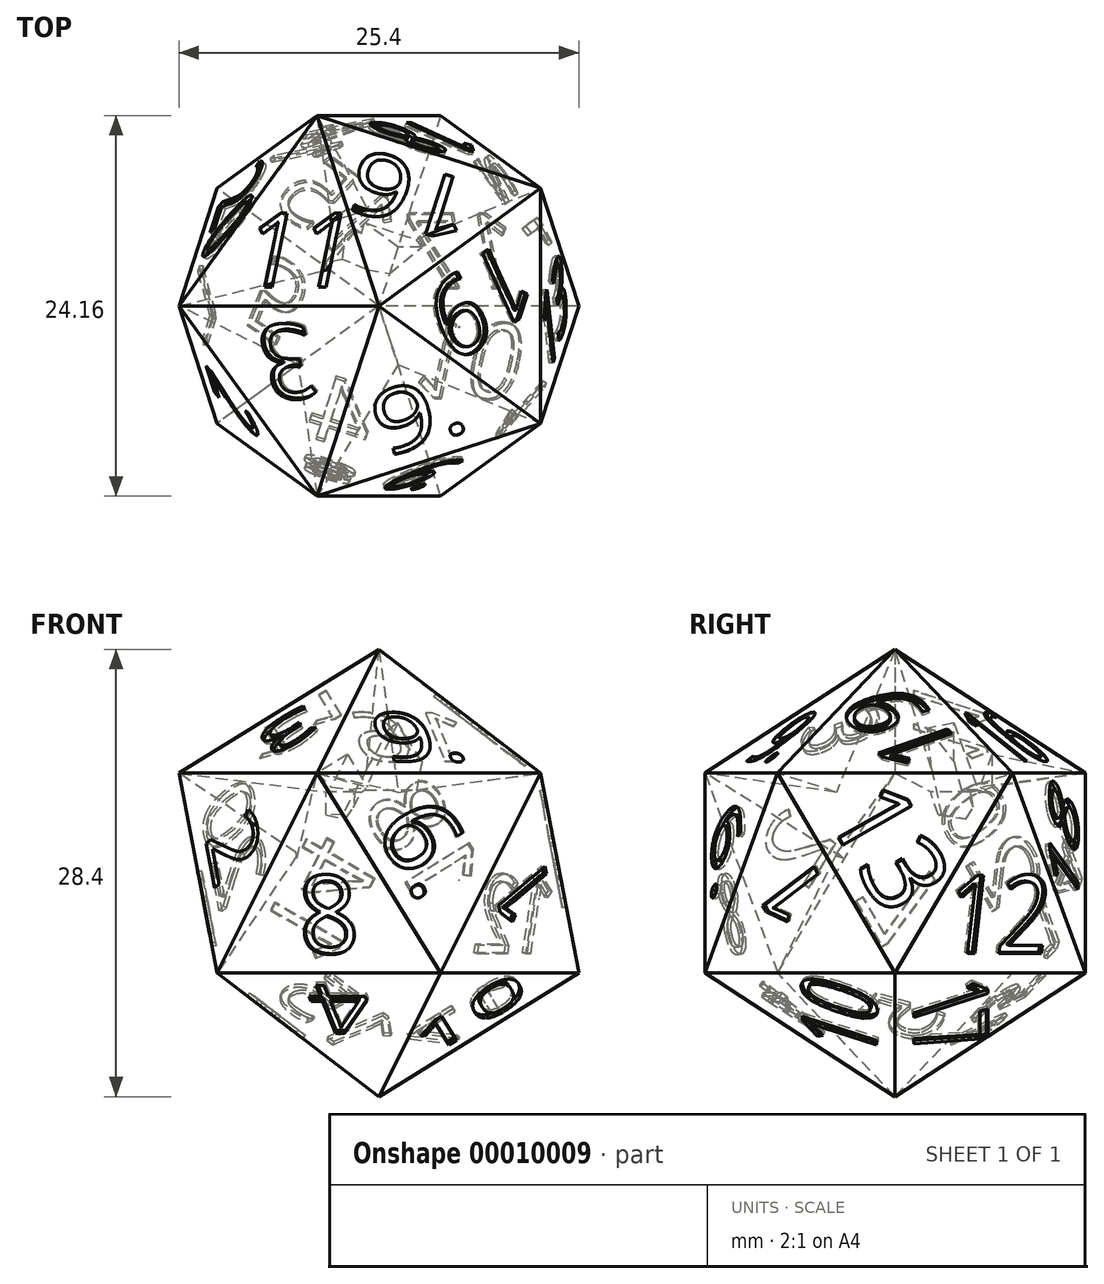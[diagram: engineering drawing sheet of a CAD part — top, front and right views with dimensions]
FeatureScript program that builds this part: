
annotation { "Feature Type Name" : "Feature", "Feature Type Description" : "" }
export const myFeature = defineFeature(function(context is Context, id is Id, definition is map)
    precondition{}
    {
        {
            var Q0;
            Q0=qCreatedBy(makeId("Top.planeOp"),FACE);
            var sketch = newSketch(context, id + "F0", { "sketchPlane" : qUnion([Q0])});
            skCircle(sketch, "E0.cCircle", {"center": v(0, 0) * mm, "radius": 12.7 * mm, "construction": true});
            skLineSegment(sketch, "E0.0", {"start": v(10.27, 7.46) * mm, "end": v(10.27, -7.46) * mm});
            skLineSegment(sketch, "E0.1", {"start": v(10.27, -7.46) * mm, "end": v(-3.92, -12.08) * mm});
            skLineSegment(sketch, "E0.2", {"start": v(-3.92, -12.08) * mm, "end": v(-12.7, 0) * mm});
            skLineSegment(sketch, "E0.3", {"start": v(-12.7, 0) * mm, "end": v(-3.92, 12.08) * mm});
            skLineSegment(sketch, "E0.4", {"start": v(-3.92, 12.08) * mm, "end": v(10.27, 7.46) * mm});
            skLineSegment(sketch, "E1", {"start": v(0, 0) * mm, "end": v(-3.92, -12.08) * mm, "construction": true});
            skSolve(sketch);
        }
        {
            var Q0;
            Q0=qCreatedBy(makeId("Right.planeOp"),FACE);
            var sketch = newSketch(context, id + "F1", { "sketchPlane" : qUnion([Q0])});
            skLineSegment(sketch, "E2", {"start": v(0, 0) * mm, "end": v(0, 7.85) * mm, "construction": true});
            skSolve(sketch);
        }
        {
            var Q0;
            Q0=sQuery(id+"F0.wireOp",VERTEX,"E0.1.start");
            var Q1;
            Q1=sQuery(id+"F0.wireOp",VERTEX,"E0.2.start");
            var Q2;
            Q2=sQuery(id+"F1.wireOp",VERTEX,"E2.end");
            cPlane(context, id + "F2", {"entities" : qUnion([Q0, Q1, Q2]), "cplaneType" : CPlaneType.THREE_POINT, "offset" : 152.4 * mm, "width" : 152.4 * mm, "height" : 152.4 * mm});
        }
        {
            var Q0;
            Q0=qCreatedBy(id+"F2.planeOp",FACE);
            var sketch = newSketch(context, id + "F3", { "sketchPlane" : qUnion([Q0])});
            skPoint(sketch, "E3.0", {"position": v(-5.19, -9.77) * mm});
            skPoint(sketch, "E4.0", {"position": v(9.27, -6.04) * mm});
            skPoint(sketch, "E5.0", {"position": v(-1.2, 4.61) * mm});
            skLineSegment(sketch, "E6", {"start": v(-5.19, -9.77) * mm, "end": v(-1.2, 4.61) * mm});
            skLineSegment(sketch, "E7", {"start": v(9.27, -6.04) * mm, "end": v(-1.2, 4.61) * mm});
            skLineSegment(sketch, "E8", {"start": v(9.27, -6.04) * mm, "end": v(-5.19, -9.77) * mm});
            skLineSegment(sketch, "E9", {"start": v(-3.19, -2.58) * mm, "end": v(9.27, -6.04) * mm, "construction": true});
            skSolve(sketch);
        }
        {
            var Q0;
            Q0=sQuery(id+"F3.wireOp",VERTEX,"E3.0");
            var Q1;
            Q1=sQuery(id+"F0.wireOp",VERTEX,"E0.2.end");
            var Q2;
            Q2=sQuery(id+"F1.wireOp",VERTEX,"E2.end");
            cPlane(context, id + "F4", {"entities" : qUnion([Q0, Q1, Q2]), "cplaneType" : CPlaneType.THREE_POINT, "offset" : 152.4 * mm, "width" : 152.4 * mm, "height" : 152.4 * mm});
        }
        {
            var Q0;
            Q0=qCreatedBy(id+"F4.planeOp",FACE);
            var sketch = newSketch(context, id + "F5", { "sketchPlane" : qUnion([Q0])});
            skPoint(sketch, "E10.0", {"position": v(-11.06, 0) * mm});
            skPoint(sketch, "E11.0", {"position": v(-0.99, -11.02) * mm});
            skPoint(sketch, "E12.0", {"position": v(3.52, 3.21) * mm});
            skLineSegment(sketch, "E13", {"start": v(-11.06, 0) * mm, "end": v(3.52, 3.21) * mm});
            skLineSegment(sketch, "E14", {"start": v(-0.99, -11.02) * mm, "end": v(-11.06, 0) * mm});
            skLineSegment(sketch, "E15", {"start": v(-0.99, -11.02) * mm, "end": v(3.52, 3.21) * mm});
            skLineSegment(sketch, "E16", {"start": v(-11.06, 0) * mm, "end": v(1.26, -3.9) * mm, "construction": true});
            skLineSegment(sketch, "E17", {"start": v(3.52, 3.21) * mm, "end": v(-6.03, -5.5) * mm, "construction": true});
            skSolve(sketch);
        }
        {
            var Q0;
            Q0=sQuery(id+"F5.wireOp",VERTEX,"E10.0");
            var Q1;
            Q1=sQuery(id+"F0.wireOp",VERTEX,"E0.3.end");
            var Q2;
            Q2=sQuery(id+"F3.wireOp",VERTEX,"E5.0");
            cPlane(context, id + "F6", {"entities" : qUnion([Q0, Q1, Q2]), "cplaneType" : CPlaneType.THREE_POINT, "offset" : 152.4 * mm, "width" : 152.4 * mm, "height" : 152.4 * mm});
        }
        {
            var Q0;
            Q0=qCreatedBy(id+"F6.planeOp",FACE);
            var sketch = newSketch(context, id + "F7", { "sketchPlane" : qUnion([Q0])});
            skPoint(sketch, "E18.0", {"position": v(-0.99, 11.02) * mm});
            skPoint(sketch, "E19.0", {"position": v(-11.06, 0) * mm});
            skPoint(sketch, "E20.0", {"position": v(3.52, -3.21) * mm});
            skLineSegment(sketch, "E21", {"start": v(-0.99, 11.02) * mm, "end": v(3.52, -3.21) * mm});
            skLineSegment(sketch, "E22", {"start": v(3.52, -3.21) * mm, "end": v(-11.06, 0) * mm});
            skLineSegment(sketch, "E23", {"start": v(-0.99, 11.02) * mm, "end": v(-11.06, 0) * mm});
            skLineSegment(sketch, "E24", {"start": v(-6.03, 5.5) * mm, "end": v(3.52, -3.21) * mm, "construction": true});
            skSolve(sketch);
        }
        {
            var Q0;
            Q0=sQuery(id+"F0.wireOp",VERTEX,"E0.4.end");
            var Q1;
            Q1=sQuery(id+"F3.wireOp",VERTEX,"E5.0");
            var Q2;
            Q2=sQuery(id+"F0.wireOp",VERTEX,"E0.3.end");
            cPlane(context, id + "F8", {"entities" : qUnion([Q0, Q1, Q2]), "cplaneType" : CPlaneType.THREE_POINT, "offset" : 152.4 * mm, "width" : 152.4 * mm, "height" : 152.4 * mm});
        }
        {
            var Q0;
            Q0=qCreatedBy(id+"F8.planeOp",FACE);
            var sketch = newSketch(context, id + "F9", { "sketchPlane" : qUnion([Q0])});
            skPoint(sketch, "E25.0", {"position": v(-5.19, 9.77) * mm});
            skPoint(sketch, "E26.0", {"position": v(9.27, 6.04) * mm});
            skPoint(sketch, "E27.0", {"position": v(-1.2, -4.61) * mm});
            skLineSegment(sketch, "E28", {"start": v(9.27, 6.04) * mm, "end": v(-1.2, -4.61) * mm});
            skLineSegment(sketch, "E29", {"start": v(-1.2, -4.61) * mm, "end": v(-5.19, 9.77) * mm});
            skLineSegment(sketch, "E30", {"start": v(-5.19, 9.77) * mm, "end": v(9.27, 6.04) * mm});
            skSolve(sketch);
        }
        {
            var Q0;
            Q0=sQuery(id+"F0.wireOp",VERTEX,"E0.4.end");
            var Q1;
            Q1=sQuery(id+"F3.wireOp",VERTEX,"E5.0");
            var Q2;
            Q2=sQuery(id+"F3.wireOp",VERTEX,"E4.0");
            cPlane(context, id + "F10", {"entities" : qUnion([Q0, Q1, Q2]), "cplaneType" : CPlaneType.THREE_POINT, "offset" : 152.4 * mm, "width" : 152.4 * mm, "height" : 152.4 * mm});
        }
        {
            var Q0;
            Q0=qCreatedBy(id+"F10.planeOp",FACE);
            var sketch = newSketch(context, id + "F11", { "sketchPlane" : qUnion([Q0])});
            skPoint(sketch, "E31.0", {"position": v(8.16, 7.46) * mm});
            skPoint(sketch, "E32.0", {"position": v(-4.76, 0) * mm});
            skPoint(sketch, "E33.0", {"position": v(8.16, -7.46) * mm});
            skLineSegment(sketch, "E34", {"start": v(8.16, 7.46) * mm, "end": v(8.16, -7.46) * mm});
            skLineSegment(sketch, "E35", {"start": v(8.16, -7.46) * mm, "end": v(-4.76, 0) * mm});
            skLineSegment(sketch, "E36", {"start": v(8.16, 7.46) * mm, "end": v(-4.76, 0) * mm});
            skSolve(sketch);
        }
        {
            var Q0;
            Q0=sQuery(id+"F5.wireOp",EDGE,"E14");
            cPlane(context, id + "F12", {"entities" : qUnion([Q0]), "cplaneType" : CPlaneType.LINE_ANGLE, "offset" : 152.4 * mm, "angle" : 100.81 * degree, "width" : 152.4 * mm, "height" : 152.4 * mm});
        }
        {
            var Q0;
            Q0=qCreatedBy(id+"F12.planeOp",FACE);
            var sketch = newSketch(context, id + "F13", { "sketchPlane" : qUnion([Q0])});
            skLineSegment(sketch, "E37", {"start": v(7.14, -2.92) * mm, "end": v(-7.66, -0.9) * mm});
            skPoint(sketch, "E38.orphan", {"position": v(-2, -14.73) * mm});
            skPoint(sketch, "E39.start.orphan", {"position": v(-0.26, -1.91) * mm});
            skPoint(sketch, "E40.start.orphan", {"position": v(2.56, -8.82) * mm});
            skLineSegment(sketch, "E41", {"start": v(7.14, -2.92) * mm, "end": v(-2, -14.72) * mm});
            skLineSegment(sketch, "E42", {"start": v(-7.66, -0.9) * mm, "end": v(-2, -14.72) * mm});
            skLineSegment(sketch, "E43", {"start": v(-0.26, -1.91) * mm, "end": v(-2, -14.72) * mm, "construction": true});
            skLineSegment(sketch, "E44", {"start": v(-4.83, -7.81) * mm, "end": v(7.14, -2.92) * mm, "construction": true});
            skSolve(sketch);
        }
        {
            var Q0;
            Q0=makeQuery(id+"F7.imprint","IMPRINT",FACE,{"disambiguationData":[TD([[makeQuery(id+"F7.imprint","IMPRINT",EDGE,{"derivedFrom":sQuery(id+"F7.wireOp",EDGE,"E21")}),-1.0]])]});
            extrude(context, id + "F14", {"entities" : qUnion([Q0]), "oppositeDirection" : true, "depth" : 2 / 76.2 * mm});
        }
        {
            var Q0;
            Q0=makeQuery(id+"F9.imprint","IMPRINT",FACE,{"disambiguationData":[TD([[makeQuery(id+"F9.imprint","IMPRINT",EDGE,{"derivedFrom":sQuery(id+"F9.wireOp",EDGE,"E28")}),-1.0]])]});
            extrude(context, id + "F15", {"entities" : qUnion([Q0]), "operationType" : NewBodyOperationType.ADD, "oppositeDirection" : true, "depth" : 2 / 76.2 * mm});
        }
        {
            var Q0;
            Q0=makeQuery(id+"F11.imprint","IMPRINT",FACE,{"disambiguationData":[TD([[makeQuery(id+"F11.imprint","IMPRINT",EDGE,{"derivedFrom":sQuery(id+"F11.wireOp",EDGE,"E34")}),-1.0]])]});
            extrude(context, id + "F16", {"entities" : qUnion([Q0]), "operationType" : NewBodyOperationType.ADD, "depth" : 16.93 * mm});
        }
        {
            var Q0;
            Q0=makeQuery(id+"F3.imprint","IMPRINT",FACE,{"disambiguationData":[TD([[makeQuery(id+"F3.imprint","IMPRINT",EDGE,{"derivedFrom":sQuery(id+"F3.wireOp",EDGE,"E6")}),-1.0]])]});
            extrude(context, id + "F17", {"entities" : qUnion([Q0]), "operationType" : NewBodyOperationType.ADD, "oppositeDirection" : true, "depth" : 2 / 76.2 * mm});
        }
        {
            var Q0;
            Q0=makeQuery(id+"F5.imprint","IMPRINT",FACE,{"disambiguationData":[TD([[makeQuery(id+"F5.imprint","IMPRINT",EDGE,{"derivedFrom":sQuery(id+"F5.wireOp",EDGE,"E13")}),-1.0]])]});
            extrude(context, id + "F18", {"entities" : qUnion([Q0]), "operationType" : NewBodyOperationType.ADD, "oppositeDirection" : true, "depth" : 18.55 * mm});
        }
        {
            var Q0;
            Q0 = qSketchRegion(id + "F13", true);
            extrude(context, id + "F19", {"entities" : qUnion([Q0]), "operationType" : NewBodyOperationType.ADD, "depth" : 2 / 76.2 * mm});
        }
        {
            var Q0;
            Q0=makeQuery(id+"F19.opExtrude","CAP_EDGE",EDGE,{"disambiguationData":[OSD([sQuery(id+"F13.wireOp",EDGE,"E42")])],"isStart":true});
            cPlane(context, id + "F20", {"entities" : qUnion([Q0]), "cplaneType" : CPlaneType.LINE_ANGLE, "offset" : 152.4 * mm, "angle" : 100.81 * degree, "width" : 152.4 * mm, "height" : 152.4 * mm});
        }
        {
            var Q0;
            Q0=qCreatedBy(id+"F20.planeOp",FACE);
            var sketch = newSketch(context, id + "F21", { "sketchPlane" : qUnion([Q0])});
            skLineSegment(sketch, "E45.0", {"start": v(0.15, 2.38) * mm, "end": v(6.81, -10.98) * mm});
            skLineSegment(sketch, "E46", {"start": v(6.81, -10.98) * mm, "end": v(-8.1, -10.07) * mm});
            skLineSegment(sketch, "E47", {"start": v(-8.1, -10.07) * mm, "end": v(0.15, 2.38) * mm});
            skLineSegment(sketch, "E48", {"start": v(-8.1, -10.07) * mm, "end": v(3.48, -4.3) * mm, "construction": true});
            skSolve(sketch);
        }
        {
            var Q0;
            Q0 = qSketchRegion(id + "F21", true);
            extrude(context, id + "F22", {"entities" : qUnion([Q0]), "operationType" : NewBodyOperationType.ADD, "depth" : 16.93 * mm});
        }
        {
            var Q0;
            Q0=sQuery(id+"F5.wireOp",VERTEX,"E11.0");
            var Q1;
            Q1=sQuery(id+"F3.wireOp",VERTEX,"E4.0");
            var Q2;
            Q2=makeQuery(id+"F22.opExtrude","CAP_VERTEX",VERTEX,{"disambiguationData":[OSD([sQuery(id+"F21.wireOp",EDGE,"E46"),sQuery(id+"F21.wireOp",EDGE,"E47")])],"isStart":true});
            cPlane(context, id + "F23", {"entities" : qUnion([Q0, Q1, Q2]), "cplaneType" : CPlaneType.THREE_POINT, "offset" : 152.4 * mm, "width" : 152.4 * mm, "height" : 152.4 * mm});
        }
        {
            var Q0;
            Q0=qCreatedBy(id+"F23.planeOp",FACE);
            var sketch = newSketch(context, id + "F24", { "sketchPlane" : qUnion([Q0])});
            skLineSegment(sketch, "E49.0", {"start": v(0.9, -14.83) * mm, "end": v(-7.33, -2.38) * mm});
            skLineSegment(sketch, "E50.0", {"start": v(7.57, -1.47) * mm, "end": v(-7.33, -2.38) * mm});
            skLineSegment(sketch, "E51", {"start": v(0.9, -14.83) * mm, "end": v(7.57, -1.47) * mm});
            skLineSegment(sketch, "E52", {"start": v(4.24, -8.15) * mm, "end": v(-7.33, -2.38) * mm, "construction": true});
            skSolve(sketch);
        }
        {
            var Q0;
            Q0=makeQuery(id+"F24.imprint","IMPRINT",FACE,{"disambiguationData":[TD([[makeQuery(id+"F24.imprint","IMPRINT",EDGE,{"derivedFrom":sQuery(id+"F24.wireOp",EDGE,"E49.0")}),-1.0]])]});
            extrude(context, id + "F25", {"entities" : qUnion([Q0]), "operationType" : NewBodyOperationType.ADD, "oppositeDirection" : true, "depth" : 16.93 * mm});
        }
        {
            var Q0;
            Q0=makeQuery(id+"F14.opExtrude","CAP_EDGE",EDGE,{"disambiguationData":[OSD([sQuery(id+"F7.wireOp",EDGE,"E23")])],"isStart":true});
            cPlane(context, id + "F26", {"entities" : qUnion([Q0]), "cplaneType" : CPlaneType.LINE_ANGLE, "offset" : 152.4 * mm, "angle" : 79.18 * degree, "width" : 152.4 * mm, "height" : 152.4 * mm});
        }
        {
            var Q0;
            Q0=qCreatedBy(id+"F26.planeOp",FACE);
            var sketch = newSketch(context, id + "F27", { "sketchPlane" : qUnion([Q0])});
            skLineSegment(sketch, "E53.0", {"start": v(7.66, -0.9) * mm, "end": v(-7.14, -2.92) * mm});
            skLineSegment(sketch, "E54", {"start": v(7.66, -0.9) * mm, "end": v(2, -14.72) * mm});
            skLineSegment(sketch, "E55", {"start": v(2, -14.72) * mm, "end": v(-7.14, -2.92) * mm});
            skLineSegment(sketch, "E56", {"start": v(2, -14.72) * mm, "end": v(0.26, -1.91) * mm, "construction": true});
            skLineSegment(sketch, "E57", {"start": v(4.83, -7.81) * mm, "end": v(-7.14, -2.92) * mm, "construction": true});
            skSolve(sketch);
        }
        {
            var Q0;
            Q0 = qSketchRegion(id + "F27", true);
            extrude(context, id + "F28", {"entities" : qUnion([Q0]), "operationType" : NewBodyOperationType.ADD, "depth" : 6.35 * mm});
        }
        {
            var Q0;
            Q0=sQuery(id+"F7.wireOp",VERTEX,"E19.0");
            var Q1;
            Q1=makeQuery(id+"F22.boolean.opBoolean","MERGE",VERTEX,{"derivedFrom":[makeQuery(id+"F19.opExtrude","CAP_VERTEX",VERTEX,{"disambiguationData":[OSD([sQuery(id+"F13.wireOp",EDGE,"E41"),sQuery(id+"F13.wireOp",EDGE,"E42")])],"isStart":true}),makeQuery(id+"F22.opExtrude","CAP_VERTEX",VERTEX,{"disambiguationData":[OSD([sQuery(id+"F21.wireOp",EDGE,"E45.0"),sQuery(id+"F21.wireOp",EDGE,"E46")])],"isStart":true})]});
            var Q2;
            Q2=sQuery(id+"F27.wireOp",VERTEX,"E54.end");
            cPlane(context, id + "F29", {"entities" : qUnion([Q0, Q1, Q2]), "cplaneType" : CPlaneType.THREE_POINT, "offset" : 152.4 * mm, "width" : 152.4 * mm, "height" : 152.4 * mm});
        }
        {
            var Q0;
            Q0=qCreatedBy(id+"F29.planeOp",FACE);
            var sketch = newSketch(context, id + "F30", { "sketchPlane" : qUnion([Q0])});
            skLineSegment(sketch, "E58.0", {"start": v(0, 2.38) * mm, "end": v(7.46, -10.55) * mm});
            skLineSegment(sketch, "E59.0", {"start": v(-7.47, -10.55) * mm, "end": v(0, 2.38) * mm});
            skLineSegment(sketch, "E60", {"start": v(-7.47, -10.55) * mm, "end": v(7.46, -10.55) * mm});
            skSolve(sketch);
        }
        {
            var Q0;
            Q0=makeQuery(id+"F30.imprint","IMPRINT",FACE,{"disambiguationData":[TD([[makeQuery(id+"F30.imprint","IMPRINT",EDGE,{"derivedFrom":sQuery(id+"F30.wireOp",EDGE,"E58.0")}),-1.0]])]});
            extrude(context, id + "F31", {"entities" : qUnion([Q0]), "operationType" : NewBodyOperationType.ADD, "oppositeDirection" : true, "depth" : 6.35 * mm});
        }
        {
            var Q0;
            Q0=sQuery(id+"F27.wireOp",EDGE,"E54");
            cPlane(context, id + "F32", {"entities" : qUnion([Q0]), "cplaneType" : CPlaneType.LINE_ANGLE, "offset" : 152.4 * mm, "angle" : 79.19 * degree, "width" : 152.4 * mm, "height" : 152.4 * mm});
        }
        {
            var Q0;
            Q0=qCreatedBy(id+"F32.planeOp",FACE);
            var sketch = newSketch(context, id + "F33", { "sketchPlane" : qUnion([Q0])});
            skLineSegment(sketch, "E61.0", {"start": v(0.15, 2.38) * mm, "end": v(6.81, -10.98) * mm});
            skLineSegment(sketch, "E62", {"start": v(0.15, 2.38) * mm, "end": v(-8.1, -10.08) * mm});
            skLineSegment(sketch, "E63", {"start": v(-8.1, -10.08) * mm, "end": v(6.81, -10.98) * mm});
            skLineSegment(sketch, "E64", {"start": v(-8.1, -10.08) * mm, "end": v(3.48, -4.3) * mm, "construction": true});
            skLineSegment(sketch, "E65", {"start": v(0.15, 2.38) * mm, "end": v(-0.64, -10.53) * mm, "construction": true});
            skSolve(sketch);
        }
        {
            var Q0;
            Q0 = qSketchRegion(id + "F33", true);
            extrude(context, id + "F34", {"entities" : qUnion([Q0]), "operationType" : NewBodyOperationType.ADD, "oppositeDirection" : true, "depth" : 6.35 * mm});
        }
        {
            var Q0;
            Q0=sQuery(id+"F33.wireOp",EDGE,"E63");
            cPlane(context, id + "F35", {"entities" : qUnion([Q0]), "cplaneType" : CPlaneType.LINE_ANGLE, "offset" : 152.4 * mm, "angle" : 52.62 * degree, "width" : 152.4 * mm, "height" : 152.4 * mm});
        }
        {
            var Q0;
            Q0=qCreatedBy(id+"F35.planeOp",FACE);
            var sketch = newSketch(context, id + "F36", { "sketchPlane" : qUnion([Q0])});
            skLineSegment(sketch, "E66.0", {"start": v(7.11, 2.3) * mm, "end": v(-7.34, -1.43) * mm});
            skLineSegment(sketch, "E67", {"start": v(7.11, 2.3) * mm, "end": v(3.12, -12.08) * mm});
            skLineSegment(sketch, "E68", {"start": v(3.12, -12.08) * mm, "end": v(-7.34, -1.43) * mm});
            skLineSegment(sketch, "E69", {"start": v(-0.11, 0.44) * mm, "end": v(3.12, -12.08) * mm, "construction": true});
            skLineSegment(sketch, "E70", {"start": v(-7.34, -1.43) * mm, "end": v(5.12, -4.89) * mm, "construction": true});
            skSolve(sketch);
        }
        {
            var Q0;
            Q0 = qSketchRegion(id + "F36", true);
            extrude(context, id + "F37", {"entities" : qUnion([Q0]), "operationType" : NewBodyOperationType.ADD, "depth" : 6.35 * mm});
        }
        {
            var Q0;
            Q0=sQuery(id+"F36.wireOp",EDGE,"E67");
            cPlane(context, id + "F38", {"entities" : qUnion([Q0]), "cplaneType" : CPlaneType.LINE_ANGLE, "offset" : 152.4 * mm, "angle" : 30.6 * degree, "width" : 152.4 * mm, "height" : 152.4 * mm});
        }
        {
            var Q0;
            Q0=qCreatedBy(id+"F38.planeOp",FACE);
            var sketch = newSketch(context, id + "F39", { "sketchPlane" : qUnion([Q0])});
            skLineSegment(sketch, "E71.0", {"start": v(-4.7, -5.82) * mm, "end": v(-9.2, 8.42) * mm});
            skLineSegment(sketch, "E72", {"start": v(-4.7, -5.82) * mm, "end": v(5.37, 5.2) * mm});
            skLineSegment(sketch, "E73", {"start": v(5.37, 5.2) * mm, "end": v(-9.2, 8.42) * mm});
            skLineSegment(sketch, "E74", {"start": v(-6.96, 1.3) * mm, "end": v(5.37, 5.2) * mm, "construction": true});
            skSolve(sketch);
        }
        {
            var Q0;
            Q0 = qSketchRegion(id + "F39", true);
            extrude(context, id + "F40", {"entities" : qUnion([Q0]), "operationType" : NewBodyOperationType.ADD, "oppositeDirection" : true, "depth" : 6.35 * mm});
        }
        {
            var Q0;
            Q0=sQuery(id+"F36.wireOp",VERTEX,"E66.0.start");
            var Q1;
            Q1=makeQuery(id+"F34.boolean.opBoolean","MERGE",VERTEX,{"derivedFrom":[makeQuery(id+"F28.boolean.opBoolean","MERGE",VERTEX,{"derivedFrom":[makeQuery(id+"F15.boolean.opBoolean","MERGE",VERTEX,{"derivedFrom":[makeQuery(id+"F14.opExtrude","CAP_VERTEX",VERTEX,{"disambiguationData":[OSD([sQuery(id+"F7.wireOp",EDGE,"E21"),sQuery(id+"F7.wireOp",EDGE,"E23")])],"isStart":true}),makeQuery(id+"F15.opExtrude","CAP_VERTEX",VERTEX,{"disambiguationData":[OSD([sQuery(id+"F9.wireOp",EDGE,"E29"),sQuery(id+"F9.wireOp",EDGE,"E30")])],"isStart":true})]}),makeQuery(id+"F28.opExtrude","CAP_VERTEX",VERTEX,{"disambiguationData":[OSD([sQuery(id+"F27.wireOp",EDGE,"E53.0"),sQuery(id+"F27.wireOp",EDGE,"E54")])],"isStart":true})]}),makeQuery(id+"F34.opExtrude","CAP_VERTEX",VERTEX,{"disambiguationData":[OSD([sQuery(id+"F33.wireOp",EDGE,"E61.0"),sQuery(id+"F33.wireOp",EDGE,"E62")])],"isStart":true})]});
            var Q2;
            Q2=makeQuery(id+"F16.boolean.opBoolean","MERGE",VERTEX,{"derivedFrom":[makeQuery(id+"F15.opExtrude","CAP_VERTEX",VERTEX,{"disambiguationData":[OSD([sQuery(id+"F9.wireOp",EDGE,"E28"),sQuery(id+"F9.wireOp",EDGE,"E30")])],"isStart":true}),makeQuery(id+"F16.opExtrude","CAP_VERTEX",VERTEX,{"disambiguationData":[OSD([sQuery(id+"F11.wireOp",EDGE,"E34"),sQuery(id+"F11.wireOp",EDGE,"E35")])],"isStart":true})]});
            cPlane(context, id + "F41", {"entities" : qUnion([Q0, Q1, Q2]), "cplaneType" : CPlaneType.THREE_POINT, "offset" : 152.4 * mm, "width" : 152.4 * mm, "height" : 152.4 * mm});
        }
        {
            var Q0;
            Q0=qCreatedBy(id+"F41.planeOp",FACE);
            var sketch = newSketch(context, id + "F42", { "sketchPlane" : qUnion([Q0])});
            skLineSegment(sketch, "E75.0", {"start": v(-7.33, -2.38) * mm, "end": v(7.57, -1.47) * mm});
            skLineSegment(sketch, "E76.0", {"start": v(-7.33, -2.38) * mm, "end": v(0.9, -14.83) * mm});
            skLineSegment(sketch, "E77", {"start": v(0.9, -14.83) * mm, "end": v(7.57, -1.47) * mm});
            skSolve(sketch);
        }
        {
            var Q0;
            Q0 = qSketchRegion(id + "F42", true);
            extrude(context, id + "F43", {"entities" : qUnion([Q0]), "operationType" : NewBodyOperationType.ADD, "depth" : 6.35 * mm});
        }
        {
            var Q0;
            Q0=sQuery(id+"F36.wireOp",VERTEX,"E66.0.start");
            var Q1;
            Q1=makeQuery(id+"F40.opExtrude","CAP_VERTEX",VERTEX,{"disambiguationData":[OSD([sQuery(id+"F39.wireOp",EDGE,"E72"),sQuery(id+"F39.wireOp",EDGE,"E73")])],"isStart":true});
            var Q2;
            Q2=makeQuery(id+"F43.boolean.opBoolean","MERGE",VERTEX,{"derivedFrom":[makeQuery(id+"F16.boolean.opBoolean","MERGE",VERTEX,{"derivedFrom":[makeQuery(id+"F15.opExtrude","CAP_VERTEX",VERTEX,{"disambiguationData":[OSD([sQuery(id+"F9.wireOp",EDGE,"E28"),sQuery(id+"F9.wireOp",EDGE,"E30")])],"isStart":true}),makeQuery(id+"F16.opExtrude","CAP_VERTEX",VERTEX,{"disambiguationData":[OSD([sQuery(id+"F11.wireOp",EDGE,"E34"),sQuery(id+"F11.wireOp",EDGE,"E35")])],"isStart":true})]}),makeQuery(id+"F43.opExtrude","CAP_VERTEX",VERTEX,{"disambiguationData":[OSD([sQuery(id+"F42.wireOp",EDGE,"E75.0"),sQuery(id+"F42.wireOp",EDGE,"E77")])],"isStart":true})]});
            cPlane(context, id + "F44", {"entities" : qUnion([Q0, Q1, Q2]), "cplaneType" : CPlaneType.THREE_POINT, "offset" : 152.4 * mm, "width" : 152.4 * mm, "height" : 152.4 * mm});
        }
        {
            var Q0;
            Q0=qCreatedBy(id+"F44.planeOp",FACE);
            var sketch = newSketch(context, id + "F45", { "sketchPlane" : qUnion([Q0])});
            skLineSegment(sketch, "E78.0", {"start": v(5.97, -11.46) * mm, "end": v(0.32, 2.36) * mm});
            skLineSegment(sketch, "E79.0", {"start": v(5.97, -11.46) * mm, "end": v(-8.82, -9.44) * mm});
            skLineSegment(sketch, "E80", {"start": v(0.32, 2.36) * mm, "end": v(-8.82, -9.44) * mm});
            skSolve(sketch);
        }
        {
            var Q0;
            Q0 = qSketchRegion(id + "F45", true);
            extrude(context, id + "F46", {"entities" : qUnion([Q0]), "operationType" : NewBodyOperationType.ADD, "oppositeDirection" : true, "depth" : 6.35 * mm});
        }
        {
            var Q0;
            Q0=makeQuery(id+"F46.boolean.opBoolean","MERGE",VERTEX,{"derivedFrom":[makeQuery(id+"F40.opExtrude","CAP_VERTEX",VERTEX,{"disambiguationData":[OSD([sQuery(id+"F39.wireOp",EDGE,"E72"),sQuery(id+"F39.wireOp",EDGE,"E73")])],"isStart":true}),makeQuery(id+"F46.opExtrude","CAP_VERTEX",VERTEX,{"disambiguationData":[OSD([sQuery(id+"F45.wireOp",EDGE,"E79.0"),sQuery(id+"F45.wireOp",EDGE,"E80")])],"isStart":true})]});
            var Q1;
            Q1=makeQuery(id+"F46.boolean.opBoolean","MERGE",VERTEX,{"derivedFrom":[makeQuery(id+"F43.boolean.opBoolean","MERGE",VERTEX,{"derivedFrom":[makeQuery(id+"F16.boolean.opBoolean","MERGE",VERTEX,{"derivedFrom":[makeQuery(id+"F15.opExtrude","CAP_VERTEX",VERTEX,{"disambiguationData":[OSD([sQuery(id+"F9.wireOp",EDGE,"E28"),sQuery(id+"F9.wireOp",EDGE,"E30")])],"isStart":true}),makeQuery(id+"F16.opExtrude","CAP_VERTEX",VERTEX,{"disambiguationData":[OSD([sQuery(id+"F11.wireOp",EDGE,"E34"),sQuery(id+"F11.wireOp",EDGE,"E35")])],"isStart":true})]}),makeQuery(id+"F43.opExtrude","CAP_VERTEX",VERTEX,{"disambiguationData":[OSD([sQuery(id+"F42.wireOp",EDGE,"E75.0"),sQuery(id+"F42.wireOp",EDGE,"E77")])],"isStart":true})]}),makeQuery(id+"F46.opExtrude","CAP_VERTEX",VERTEX,{"disambiguationData":[OSD([sQuery(id+"F45.wireOp",EDGE,"E78.0"),sQuery(id+"F45.wireOp",EDGE,"E80")])],"isStart":true})]});
            var Q2;
            Q2=makeQuery(id+"F25.boolean.opBoolean","MERGE",VERTEX,{"derivedFrom":[makeQuery(id+"F17.boolean.opBoolean","MERGE",VERTEX,{"derivedFrom":[makeQuery(id+"F16.opExtrude","CAP_VERTEX",VERTEX,{"disambiguationData":[OSD([sQuery(id+"F11.wireOp",EDGE,"E34"),sQuery(id+"F11.wireOp",EDGE,"E36")])],"isStart":true}),makeQuery(id+"F17.opExtrude","CAP_VERTEX",VERTEX,{"disambiguationData":[OSD([sQuery(id+"F3.wireOp",EDGE,"E7"),sQuery(id+"F3.wireOp",EDGE,"E8")])],"isStart":true})]}),makeQuery(id+"F25.opExtrude","CAP_VERTEX",VERTEX,{"disambiguationData":[OSD([sQuery(id+"F24.wireOp",EDGE,"E50.0"),sQuery(id+"F24.wireOp",EDGE,"E51")])],"isStart":true})]});
            cPlane(context, id + "F47", {"entities" : qUnion([Q0, Q1, Q2]), "cplaneType" : CPlaneType.THREE_POINT, "offset" : 152.4 * mm, "width" : 152.4 * mm, "height" : 152.4 * mm});
        }
        {
            var Q0;
            Q0=qCreatedBy(id+"F47.planeOp",FACE);
            var sketch = newSketch(context, id + "F48", { "sketchPlane" : qUnion([Q0])});
            skLineSegment(sketch, "E81.0", {"start": v(-7.46, -1.93) * mm, "end": v(0, -14.86) * mm});
            skLineSegment(sketch, "E82.0", {"start": v(7.46, -1.93) * mm, "end": v(-7.46, -1.93) * mm});
            skLineSegment(sketch, "E83", {"start": v(0, -14.86) * mm, "end": v(7.46, -1.93) * mm});
            skSolve(sketch);
        }
        {
            var Q0;
            Q0 = qSketchRegion(id + "F48", true);
            extrude(context, id + "F49", {"entities" : qUnion([Q0]), "operationType" : NewBodyOperationType.ADD, "depth" : 6.35 * mm});
        }
        {
            var Q0;
            Q0=makeQuery(id+"F49.boolean.opBoolean","MERGE",VERTEX,{"derivedFrom":[makeQuery(id+"F46.boolean.opBoolean","MERGE",VERTEX,{"derivedFrom":[makeQuery(id+"F40.opExtrude","CAP_VERTEX",VERTEX,{"disambiguationData":[OSD([sQuery(id+"F39.wireOp",EDGE,"E72"),sQuery(id+"F39.wireOp",EDGE,"E73")])],"isStart":true}),makeQuery(id+"F46.opExtrude","CAP_VERTEX",VERTEX,{"disambiguationData":[OSD([sQuery(id+"F45.wireOp",EDGE,"E79.0"),sQuery(id+"F45.wireOp",EDGE,"E80")])],"isStart":true})]}),makeQuery(id+"F49.opExtrude","CAP_VERTEX",VERTEX,{"disambiguationData":[OSD([sQuery(id+"F48.wireOp",EDGE,"E81.0"),sQuery(id+"F48.wireOp",EDGE,"E83")])],"isStart":true})]});
            var Q1;
            Q1=makeQuery(id+"F49.boolean.opBoolean","MERGE",VERTEX,{"derivedFrom":[makeQuery(id+"F25.boolean.opBoolean","MERGE",VERTEX,{"derivedFrom":[makeQuery(id+"F17.boolean.opBoolean","MERGE",VERTEX,{"derivedFrom":[makeQuery(id+"F16.opExtrude","CAP_VERTEX",VERTEX,{"disambiguationData":[OSD([sQuery(id+"F11.wireOp",EDGE,"E34"),sQuery(id+"F11.wireOp",EDGE,"E36")])],"isStart":true}),makeQuery(id+"F17.opExtrude","CAP_VERTEX",VERTEX,{"disambiguationData":[OSD([sQuery(id+"F3.wireOp",EDGE,"E7"),sQuery(id+"F3.wireOp",EDGE,"E8")])],"isStart":true})]}),makeQuery(id+"F25.opExtrude","CAP_VERTEX",VERTEX,{"disambiguationData":[OSD([sQuery(id+"F24.wireOp",EDGE,"E50.0"),sQuery(id+"F24.wireOp",EDGE,"E51")])],"isStart":true})]}),makeQuery(id+"F49.opExtrude","CAP_VERTEX",VERTEX,{"disambiguationData":[OSD([sQuery(id+"F48.wireOp",EDGE,"E82.0"),sQuery(id+"F48.wireOp",EDGE,"E83")])],"isStart":true})]});
            var Q2;
            Q2=makeQuery(id+"F25.boolean.opBoolean","MERGE",VERTEX,{"derivedFrom":[makeQuery(id+"F22.opExtrude","CAP_VERTEX",VERTEX,{"disambiguationData":[OSD([sQuery(id+"F21.wireOp",EDGE,"E46"),sQuery(id+"F21.wireOp",EDGE,"E47")])],"isStart":true}),makeQuery(id+"F25.opExtrude","CAP_VERTEX",VERTEX,{"disambiguationData":[OSD([sQuery(id+"F24.wireOp",EDGE,"E49.0"),sQuery(id+"F24.wireOp",EDGE,"E51")])],"isStart":true})]});
            cPlane(context, id + "F50", {"entities" : qUnion([Q0, Q1, Q2]), "cplaneType" : CPlaneType.THREE_POINT, "offset" : 152.4 * mm, "width" : 152.4 * mm, "height" : 152.4 * mm});
        }
        {
            var Q0;
            Q0=qCreatedBy(id+"F50.planeOp",FACE);
            var sketch = newSketch(context, id + "F51", { "sketchPlane" : qUnion([Q0])});
            skLineSegment(sketch, "E84.0", {"start": v(-8.82, -9.44) * mm, "end": v(0.32, 2.36) * mm});
            skLineSegment(sketch, "E85.0", {"start": v(5.97, -11.46) * mm, "end": v(0.32, 2.36) * mm});
            skLineSegment(sketch, "E86", {"start": v(-8.82, -9.44) * mm, "end": v(5.97, -11.46) * mm});
            skSolve(sketch);
        }
        {
            var Q0;
            Q0 = qSketchRegion(id + "F51", true);
            extrude(context, id + "F52", {"entities" : qUnion([Q0]), "operationType" : NewBodyOperationType.ADD, "depth" : 6.35 * mm});
        }
        {
            var Q0;
            Q0=makeQuery(id+"F52.boolean.opBoolean","MERGE",VERTEX,{"derivedFrom":[makeQuery(id+"F25.boolean.opBoolean","MERGE",VERTEX,{"derivedFrom":[makeQuery(id+"F22.opExtrude","CAP_VERTEX",VERTEX,{"disambiguationData":[OSD([sQuery(id+"F21.wireOp",EDGE,"E46"),sQuery(id+"F21.wireOp",EDGE,"E47")])],"isStart":true}),makeQuery(id+"F25.opExtrude","CAP_VERTEX",VERTEX,{"disambiguationData":[OSD([sQuery(id+"F24.wireOp",EDGE,"E49.0"),sQuery(id+"F24.wireOp",EDGE,"E51")])],"isStart":true})]}),makeQuery(id+"F52.opExtrude","CAP_VERTEX",VERTEX,{"disambiguationData":[OSD([sQuery(id+"F51.wireOp",EDGE,"E85.0"),sQuery(id+"F51.wireOp",EDGE,"E86")])],"isStart":true})]});
            var Q1;
            Q1=makeQuery(id+"F31.boolean.opBoolean","MERGE",VERTEX,{"derivedFrom":[makeQuery(id+"F22.boolean.opBoolean","MERGE",VERTEX,{"derivedFrom":[makeQuery(id+"F19.opExtrude","CAP_VERTEX",VERTEX,{"disambiguationData":[OSD([sQuery(id+"F13.wireOp",EDGE,"E41"),sQuery(id+"F13.wireOp",EDGE,"E42")])],"isStart":true}),makeQuery(id+"F22.opExtrude","CAP_VERTEX",VERTEX,{"disambiguationData":[OSD([sQuery(id+"F21.wireOp",EDGE,"E45.0"),sQuery(id+"F21.wireOp",EDGE,"E46")])],"isStart":true})]}),makeQuery(id+"F31.opExtrude","CAP_VERTEX",VERTEX,{"disambiguationData":[OSD([sQuery(id+"F30.wireOp",EDGE,"E58.0"),sQuery(id+"F30.wireOp",EDGE,"E60")])],"isStart":true})]});
            var Q2;
            Q2=sQuery(id+"F36.wireOp",VERTEX,"E69.end");
            cPlane(context, id + "F53", {"entities" : qUnion([Q0, Q1, Q2]), "cplaneType" : CPlaneType.THREE_POINT, "offset" : 152.4 * mm, "width" : 152.4 * mm, "height" : 152.4 * mm});
        }
        {
            var Q0;
            Q0=qCreatedBy(id+"F53.planeOp",FACE);
            var sketch = newSketch(context, id + "F54", { "sketchPlane" : qUnion([Q0])});
            skLineSegment(sketch, "E87.0", {"start": v(-7.34, 1.43) * mm, "end": v(7.11, -2.3) * mm});
            skLineSegment(sketch, "E88", {"start": v(7.11, -2.3) * mm, "end": v(3.12, 12.08) * mm});
            skLineSegment(sketch, "E89", {"start": v(3.12, 12.08) * mm, "end": v(-7.34, 1.43) * mm});
            skSolve(sketch);
        }
        {
            var Q0;
            Q0 = qSketchRegion(id + "F54", true);
            extrude(context, id + "F55", {"entities" : qUnion([Q0]), "operationType" : NewBodyOperationType.ADD, "depth" : 6.35 * mm});
        }
        {
            var Q0;
            Q0=makeQuery(id+"F55.boolean.opBoolean","MERGE",VERTEX,{"derivedFrom":[makeQuery(id+"F52.boolean.opBoolean","MERGE",VERTEX,{"derivedFrom":[makeQuery(id+"F25.boolean.opBoolean","MERGE",VERTEX,{"derivedFrom":[makeQuery(id+"F22.opExtrude","CAP_VERTEX",VERTEX,{"disambiguationData":[OSD([sQuery(id+"F21.wireOp",EDGE,"E46"),sQuery(id+"F21.wireOp",EDGE,"E47")])],"isStart":true}),makeQuery(id+"F25.opExtrude","CAP_VERTEX",VERTEX,{"disambiguationData":[OSD([sQuery(id+"F24.wireOp",EDGE,"E49.0"),sQuery(id+"F24.wireOp",EDGE,"E51")])],"isStart":true})]}),makeQuery(id+"F52.opExtrude","CAP_VERTEX",VERTEX,{"disambiguationData":[OSD([sQuery(id+"F51.wireOp",EDGE,"E85.0"),sQuery(id+"F51.wireOp",EDGE,"E86")])],"isStart":true})]}),makeQuery(id+"F55.opExtrude","CAP_VERTEX",VERTEX,{"disambiguationData":[OSD([sQuery(id+"F54.wireOp",EDGE,"E87.0"),sQuery(id+"F54.wireOp",EDGE,"E88")])],"isStart":true})]});
            var Q1;
            Q1=makeQuery(id+"F52.boolean.opBoolean","MERGE",VERTEX,{"derivedFrom":[makeQuery(id+"F49.boolean.opBoolean","MERGE",VERTEX,{"derivedFrom":[makeQuery(id+"F46.boolean.opBoolean","MERGE",VERTEX,{"derivedFrom":[makeQuery(id+"F40.opExtrude","CAP_VERTEX",VERTEX,{"disambiguationData":[OSD([sQuery(id+"F39.wireOp",EDGE,"E72"),sQuery(id+"F39.wireOp",EDGE,"E73")])],"isStart":true}),makeQuery(id+"F46.opExtrude","CAP_VERTEX",VERTEX,{"disambiguationData":[OSD([sQuery(id+"F45.wireOp",EDGE,"E79.0"),sQuery(id+"F45.wireOp",EDGE,"E80")])],"isStart":true})]}),makeQuery(id+"F49.opExtrude","CAP_VERTEX",VERTEX,{"disambiguationData":[OSD([sQuery(id+"F48.wireOp",EDGE,"E81.0"),sQuery(id+"F48.wireOp",EDGE,"E83")])],"isStart":true})]}),makeQuery(id+"F52.opExtrude","CAP_VERTEX",VERTEX,{"disambiguationData":[OSD([sQuery(id+"F51.wireOp",EDGE,"E84.0"),sQuery(id+"F51.wireOp",EDGE,"E86")])],"isStart":true})]});
            var Q2;
            Q2=makeQuery(id+"F55.opExtrude","CAP_VERTEX",VERTEX,{"disambiguationData":[OSD([sQuery(id+"F54.wireOp",EDGE,"E88"),sQuery(id+"F54.wireOp",EDGE,"E89")])],"isStart":true});
            cPlane(context, id + "F56", {"entities" : qUnion([Q0, Q1, Q2]), "cplaneType" : CPlaneType.THREE_POINT, "offset" : 152.4 * mm, "width" : 152.4 * mm, "height" : 152.4 * mm});
        }
        {
            var Q0;
            Q0=qCreatedBy(id+"F56.planeOp",FACE);
            var sketch = newSketch(context, id + "F57", { "sketchPlane" : qUnion([Q0])});
            skLineSegment(sketch, "E90.0", {"start": v(-4.7, 5.82) * mm, "end": v(-9.2, -8.42) * mm});
            skPoint(sketch, "E91.0.end.orphan", {"position": v(-9.2, -8.42) * mm});
            skPoint(sketch, "E91.0.start.orphan", {"position": v(5.37, -5.2) * mm});
            skLineSegment(sketch, "E92", {"start": v(-4.7, 5.82) * mm, "end": v(5.37, -5.2) * mm});
            skLineSegment(sketch, "E93", {"start": v(5.37, -5.2) * mm, "end": v(-9.2, -8.42) * mm});
            skSolve(sketch);
        }
        {
            var Q0;
            Q0 = qSketchRegion(id + "F57", true);
            extrude(context, id + "F58", {"entities" : qUnion([Q0]), "operationType" : NewBodyOperationType.ADD, "oppositeDirection" : true, "depth" : 6.35 * mm});
        }
        {
            var Q0;
            Q0=makeQuery(id+"F55.boolean.opBoolean","MERGE",VERTEX,{"derivedFrom":[makeQuery(id+"F31.boolean.opBoolean","MERGE",VERTEX,{"derivedFrom":[makeQuery(id+"F22.boolean.opBoolean","MERGE",VERTEX,{"derivedFrom":[makeQuery(id+"F19.opExtrude","CAP_VERTEX",VERTEX,{"disambiguationData":[OSD([sQuery(id+"F13.wireOp",EDGE,"E41"),sQuery(id+"F13.wireOp",EDGE,"E42")])],"isStart":true}),makeQuery(id+"F22.opExtrude","CAP_VERTEX",VERTEX,{"disambiguationData":[OSD([sQuery(id+"F21.wireOp",EDGE,"E45.0"),sQuery(id+"F21.wireOp",EDGE,"E46")])],"isStart":true})]}),makeQuery(id+"F31.opExtrude","CAP_VERTEX",VERTEX,{"disambiguationData":[OSD([sQuery(id+"F30.wireOp",EDGE,"E58.0"),sQuery(id+"F30.wireOp",EDGE,"E60")])],"isStart":true})]}),makeQuery(id+"F55.opExtrude","CAP_VERTEX",VERTEX,{"disambiguationData":[OSD([sQuery(id+"F54.wireOp",EDGE,"E87.0"),sQuery(id+"F54.wireOp",EDGE,"E89")])],"isStart":true})]});
            var Q1;
            Q1=sQuery(id+"F57.wireOp",VERTEX,"E91.0.end.orphan");
            var Q2;
            Q2=sQuery(id+"F36.wireOp",VERTEX,"E68.end");
            cPlane(context, id + "F59", {"entities" : qUnion([Q0, Q1, Q2]), "cplaneType" : CPlaneType.THREE_POINT, "offset" : 152.4 * mm, "width" : 152.4 * mm, "height" : 152.4 * mm});
        }
        {
            var Q0;
            Q0=qCreatedBy(id+"F59.planeOp",FACE);
            var sketch = newSketch(context, id + "F60", { "sketchPlane" : qUnion([Q0])});
            skLineSegment(sketch, "E94.0", {"start": v(12.48, 0) * mm, "end": v(-0.45, 7.46) * mm});
            skLineSegment(sketch, "E95", {"start": v(-0.45, 7.46) * mm, "end": v(-0.45, -7.47) * mm});
            skPoint(sketch, "E96.0.start.orphan", {"position": v(12.48, 0) * mm});
            skLineSegment(sketch, "E97", {"start": v(12.48, 0) * mm, "end": v(-0.45, -7.47) * mm});
            skSolve(sketch);
        }
        {
            var Q0;
            Q0 = qSketchRegion(id + "F60", true);
            extrude(context, id + "F61", {"entities" : qUnion([Q0]), "operationType" : NewBodyOperationType.ADD, "oppositeDirection" : true, "depth" : 6.35 * mm});
        }
        {
            var Q0;
            Q0=makeQuery(id+"F28.opExtrude","CAP_FACE",FACE,{"disambiguationData":[OSD([sQuery(id+"F27.wireOp",EDGE,"E53.0"),sQuery(id+"F27.wireOp",EDGE,"E54"),sQuery(id+"F27.wireOp",EDGE,"E55")])],"isStart":true});
            var sketch = newSketch(context, id + "F62", { "sketchPlane" : qUnion([Q0])});
            skText(sketch, "E98", { "text": "20", "fontName": "OpenSans-Regular.ttf"});
            const initialGuessF62  = {"E98": [-0.0008, -0.0111, 0.61245, 0.79051, 0.00508]};
            skSetInitialGuess(sketch, initialGuessF62);
            skSolve(sketch);
        }
        {
            var Q0;
            Q0=makeQuery(id+"F14.opExtrude","CAP_FACE",FACE,{"disambiguationData":[OSD([sQuery(id+"F7.wireOp",EDGE,"E21"),sQuery(id+"F7.wireOp",EDGE,"E22"),sQuery(id+"F7.wireOp",EDGE,"E23")])],"isStart":true});
            var sketch = newSketch(context, id + "F63", { "sketchPlane" : qUnion([Q0])});
            skText(sketch, "E99", { "text": "11", "fontName": "OpenSans-Regular.ttf"});
            const initialGuessF63  = {"E99": [-0.00667, 0.00033, 0.97654, -0.21534, 0.00508]};
            skSetInitialGuess(sketch, initialGuessF63);
            skSolve(sketch);
        }
        {
            var Q0;
            Q0=makeQuery(id+"F15.opExtrude","CAP_FACE",FACE,{"disambiguationData":[OSD([sQuery(id+"F9.wireOp",EDGE,"E28"),sQuery(id+"F9.wireOp",EDGE,"E29"),sQuery(id+"F9.wireOp",EDGE,"E30")])],"isStart":true});
            var sketch = newSketch(context, id + "F64", { "sketchPlane" : qUnion([Q0])});
            skText(sketch, "E100", { "text": "16", "fontName": "OpenSans-Regular.ttf"});
            const initialGuessF64  = {"E100": [0.00546, 0.00571, -0.96824, 0.25, 0.00508]};
            skSetInitialGuess(sketch, initialGuessF64);
            skSolve(sketch);
        }
        {
            var Q0;
            Q0=makeQuery(id+"F43.opExtrude","CAP_FACE",FACE,{"disambiguationData":[OSD([sQuery(id+"F42.wireOp",EDGE,"E75.0"),sQuery(id+"F42.wireOp",EDGE,"E76.0"),sQuery(id+"F42.wireOp",EDGE,"E77")])],"isStart":true});
            var sketch = newSketch(context, id + "F65", { "sketchPlane" : qUnion([Q0])});
            skText(sketch, "E101", { "text": "18", "fontName": "OpenSans-Regular.ttf"});
            const initialGuessF65  = {"E101": [3e-05, -0.01112, 0.55168, 0.83405, 0.00508]};
            skSetInitialGuess(sketch, initialGuessF65);
            skSolve(sketch);
        }
        {
            var Q0;
            Q0=makeQuery(id+"F34.opExtrude","CAP_FACE",FACE,{"disambiguationData":[OSD([sQuery(id+"F33.wireOp",EDGE,"E61.0"),sQuery(id+"F33.wireOp",EDGE,"E62"),sQuery(id+"F33.wireOp",EDGE,"E63")])],"isStart":true});
            var sketch = newSketch(context, id + "F66", { "sketchPlane" : qUnion([Q0])});
            skText(sketch, "E102", { "text": "14\n", "fontName": "OpenSans-Regular.ttf"});
            const initialGuessF66  = {"E102": [0.00411, -0.00842, -0.44648, 0.8948, 0.00508]};
            skSetInitialGuess(sketch, initialGuessF66);
            skSolve(sketch);
        }
        {
            var Q0;
            Q0=makeQuery(id+"F18.opExtrude","CAP_FACE",FACE,{"disambiguationData":[OSD([sQuery(id+"F5.wireOp",EDGE,"E13"),sQuery(id+"F5.wireOp",EDGE,"E14"),sQuery(id+"F5.wireOp",EDGE,"E15")])],"isStart":true});
            var sketch = newSketch(context, id + "F67", { "sketchPlane" : qUnion([Q0])});
            skText(sketch, "E103", { "text": "3\n", "fontName": "OpenSans-Regular.ttf"});
            const initialGuessF67  = {"E103": [-0.00173, 0.00076, -0.97654, -0.21534, 0.00508]};
            skSetInitialGuess(sketch, initialGuessF67);
            skSolve(sketch);
        }
        {
            var Q0;
            Q0=makeQuery(id+"F16.opExtrude","CAP_FACE",FACE,{"disambiguationData":[OSD([sQuery(id+"F11.wireOp",EDGE,"E34"),sQuery(id+"F11.wireOp",EDGE,"E35"),sQuery(id+"F11.wireOp",EDGE,"E36")])],"isStart":true});
            var sketch = newSketch(context, id + "F68", { "sketchPlane" : qUnion([Q0])});
            skText(sketch, "E104", { "text": "19", "fontName": "OpenSans-Regular.ttf"});
            const initialGuessF68  = {"E104": [0.00566, 0.00455, -0.86602, -0.5, 0.00508]};
            skSetInitialGuess(sketch, initialGuessF68);
            skSolve(sketch);
        }
        {
            var Q0;
            Q0=makeQuery(id+"F46.opExtrude","CAP_FACE",FACE,{"disambiguationData":[OSD([sQuery(id+"F45.wireOp",EDGE,"E78.0"),sQuery(id+"F45.wireOp",EDGE,"E79.0"),sQuery(id+"F45.wireOp",EDGE,"E80")])],"isStart":true});
            var sketch = newSketch(context, id + "F69", { "sketchPlane" : qUnion([Q0])});
            skText(sketch, "E105", { "text": "12", "fontName": "OpenSans-Regular.ttf"});
            const initialGuessF69  = {"E105": [-0.00506, -0.00867, 0.99084, -0.13504, 0.00508]};
            skSetInitialGuess(sketch, initialGuessF69);
            skSolve(sketch);
        }
        {
            var Q0;
            Q0=makeQuery(id+"F37.opExtrude","CAP_FACE",FACE,{"disambiguationData":[OSD([sQuery(id+"F36.wireOp",EDGE,"E66.0"),sQuery(id+"F36.wireOp",EDGE,"E67"),sQuery(id+"F36.wireOp",EDGE,"E68")])],"isStart":true});
            var sketch = newSketch(context, id + "F70", { "sketchPlane" : qUnion([Q0])});
            skSolve(sketch);
        }
        {
            var Q0;
            Q0=makeQuery(id+"F70.imprint","IMPRINT",FACE,{"disambiguationData":[TD([[makeQuery(id+"F70.imprint","IMPRINT",EDGE,{"derivedFrom":makeQuery(id+"F37.opExtrude","CAP_EDGE",EDGE,{"disambiguationData":[OSD([sQuery(id+"F36.wireOp",EDGE,"E68")])],"isStart":true})}),1.0]])]});
            var sketch = newSketch(context, id + "F71", { "sketchPlane" : qUnion([Q0])});
            skText(sketch, "E106", { "text": "15", "fontName": "OpenSans-Regular.ttf"});
            const initialGuessF71  = {"E106": [0.00148, 0.0086, -0.70055, -0.7136, 0.00508]};
            skSetInitialGuess(sketch, initialGuessF71);
            skSolve(sketch);
        }
        {
            var Q0;
            Q0=makeQuery(id+"F31.opExtrude","CAP_FACE",FACE,{"disambiguationData":[OSD([sQuery(id+"F30.wireOp",EDGE,"E58.0"),sQuery(id+"F30.wireOp",EDGE,"E59.0"),sQuery(id+"F30.wireOp",EDGE,"E60")])],"isStart":true});
            var sketch = newSketch(context, id + "F72", { "sketchPlane" : qUnion([Q0])});
            skText(sketch, "E107", { "text": "7", "fontName": "OpenSans-Regular.ttf"});
            const initialGuessF72  = {"E107": [-0.00171, -0.00313, -0.50007, -0.86599, 0.00508]};
            skSetInitialGuess(sketch, initialGuessF72);
            skSolve(sketch);
        }
        {
            var Q0;
            Q0=makeQuery(id+"F61.opExtrude","CAP_FACE",FACE,{"disambiguationData":[OSD([sQuery(id+"F60.wireOp",EDGE,"E94.0"),sQuery(id+"F60.wireOp",EDGE,"E95"),sQuery(id+"F60.wireOp",EDGE,"E97")])],"isStart":true});
            var sketch = newSketch(context, id + "F73", { "sketchPlane" : qUnion([Q0])});
            skText(sketch, "E108", { "text": "5", "fontName": "OpenSans-Regular.ttf"});
            const initialGuessF73  = {"E108": [0.0038, -0.00354, 0.86603, 0.5, 0.00508]};
            skSetInitialGuess(sketch, initialGuessF73);
            skSolve(sketch);
        }
        {
            var Q0;
            Q0=makeQuery(id+"F55.opExtrude","CAP_FACE",FACE,{"disambiguationData":[OSD([sQuery(id+"F54.wireOp",EDGE,"E87.0"),sQuery(id+"F54.wireOp",EDGE,"E88"),sQuery(id+"F54.wireOp",EDGE,"E89")])],"isStart":true});
            var sketch = newSketch(context, id + "F74", { "sketchPlane" : qUnion([Q0])});
            skText(sketch, "E109", { "text": "4", "fontName": "OpenSans-Regular.ttf"});
            const initialGuessF74  = {"E109": [0.00209, -0.0003, -0.96826, -0.24996, 0.00508]};
            skSetInitialGuess(sketch, initialGuessF74);
            skSolve(sketch);
        }
        {
            var Q0;
            Q0=makeQuery(id+"F22.opExtrude","CAP_FACE",FACE,{"disambiguationData":[OSD([sQuery(id+"F21.wireOp",EDGE,"E45.0"),sQuery(id+"F21.wireOp",EDGE,"E46"),sQuery(id+"F21.wireOp",EDGE,"E47")])],"isStart":true});
            var sketch = newSketch(context, id + "F75", { "sketchPlane" : qUnion([Q0])});
            skText(sketch, "E110", { "text": "8", "fontName": "OpenSans-Regular.ttf"});
            const initialGuessF75  = {"E110": [-0.00127, -0.00937, 0.99815, 0.0608, 0.00508]};
            skSetInitialGuess(sketch, initialGuessF75);
            skSolve(sketch);
        }
        {
            var Q0;
            Q0=makeQuery(id+"F19.opExtrude","CAP_FACE",FACE,{"disambiguationData":[OSD([sQuery(id+"F13.wireOp",EDGE,"E37"),sQuery(id+"F13.wireOp",EDGE,"E41"),sQuery(id+"F13.wireOp",EDGE,"E42")])],"isStart":true});
            var sketch = newSketch(context, id + "F76", { "sketchPlane" : qUnion([Q0])});
            skText(sketch, "E111", { "text": "2", "fontName": "OpenSans-Regular.ttf"});
            const initialGuessF76  = {"E111": [-0.00268, -0.0066, 0.6124, -0.79055, 0.00508]};
            skSetInitialGuess(sketch, initialGuessF76);
            skSolve(sketch);
        }
        {
            var Q0;
            Q0=makeQuery(id+"F25.opExtrude","CAP_FACE",FACE,{"disambiguationData":[OSD([sQuery(id+"F24.wireOp",EDGE,"E49.0"),sQuery(id+"F24.wireOp",EDGE,"E50.0"),sQuery(id+"F24.wireOp",EDGE,"E51")])],"isStart":true});
            var sketch = newSketch(context, id + "F77", { "sketchPlane" : qUnion([Q0])});
            skText(sketch, "E112", { "text": "6.", "fontName": "OpenSans-Regular.ttf"});
            const initialGuessF77  = {"E112": [-0.00364, -0.00566, 0.55174, -0.83402, 0.00508]};
            skSetInitialGuess(sketch, initialGuessF77);
            skSolve(sketch);
        }
        {
            var Q0;
            Q0=makeQuery(id+"F17.opExtrude","CAP_FACE",FACE,{"disambiguationData":[OSD([sQuery(id+"F3.wireOp",EDGE,"E6"),sQuery(id+"F3.wireOp",EDGE,"E7"),sQuery(id+"F3.wireOp",EDGE,"E8")])],"isStart":true});
            var sketch = newSketch(context, id + "F78", { "sketchPlane" : qUnion([Q0])});
            skText(sketch, "E113", { "text": "9.", "fontName": "OpenSans-Regular.ttf"});
            const initialGuessF78  = {"E113": [-0.00088, -0.00735, 0.96824, 0.25, 0.00508]};
            skSetInitialGuess(sketch, initialGuessF78);
            skSolve(sketch);
        }
        {
            var Q0;
            Q0=makeQuery(id+"F52.opExtrude","CAP_FACE",FACE,{"disambiguationData":[OSD([sQuery(id+"F51.wireOp",EDGE,"E84.0"),sQuery(id+"F51.wireOp",EDGE,"E85.0"),sQuery(id+"F51.wireOp",EDGE,"E86")])],"isStart":true});
            var sketch = newSketch(context, id + "F79", { "sketchPlane" : qUnion([Q0])});
            skText(sketch, "E114", { "text": "1", "fontName": "OpenSans-Regular.ttf"});
            const initialGuessF79  = {"E114": [0.004, -0.0053, -0.61228, 0.79064, 0.00508]};
            skSetInitialGuess(sketch, initialGuessF79);
            skSolve(sketch);
        }
        {
            var Q0;
            Q0=makeQuery(id+"F49.opExtrude","CAP_FACE",FACE,{"disambiguationData":[OSD([sQuery(id+"F48.wireOp",EDGE,"E81.0"),sQuery(id+"F48.wireOp",EDGE,"E82.0"),sQuery(id+"F48.wireOp",EDGE,"E83")])],"isStart":true});
            var sketch = newSketch(context, id + "F80", { "sketchPlane" : qUnion([Q0])});
            skText(sketch, "E115", { "text": "13", "fontName": "OpenSans-Regular.ttf"});
            const initialGuessF80  = {"E115": [-0.00455, -0.00444, 0.49995, -0.86605, 0.00508]};
            skSetInitialGuess(sketch, initialGuessF80);
            skSolve(sketch);
        }
        {
            var Q0;
            Q0=makeQuery(id+"F58.opExtrude","CAP_FACE",FACE,{"disambiguationData":[OSD([sQuery(id+"F57.wireOp",EDGE,"E90.0"),sQuery(id+"F57.wireOp",EDGE,"E92"),sQuery(id+"F57.wireOp",EDGE,"E93")])],"isStart":true});
            var sketch = newSketch(context, id + "F81", { "sketchPlane" : qUnion([Q0])});
            skText(sketch, "E116", { "text": "10", "fontName": "OpenSans-Regular.ttf"});
            const initialGuessF81  = {"E116": [-0.00596, -0.0064, 0.97653, 0.21539, 0.00508]};
            skSetInitialGuess(sketch, initialGuessF81);
            skSolve(sketch);
        }
        {
            var Q0;
            Q0=makeQuery(id+"F40.opExtrude","CAP_FACE",FACE,{"disambiguationData":[OSD([sQuery(id+"F39.wireOp",EDGE,"E71.0"),sQuery(id+"F39.wireOp",EDGE,"E72"),sQuery(id+"F39.wireOp",EDGE,"E73")])],"isStart":true});
            var sketch = newSketch(context, id + "F82", { "sketchPlane" : qUnion([Q0])});
            skText(sketch, "E117", { "text": "17", "fontName": "OpenSans-Regular.ttf"});
            const initialGuessF82  = {"E117": [0.00157, 0.00474, -0.97654, 0.21531, 0.00508]};
            skSetInitialGuess(sketch, initialGuessF82);
            skSolve(sketch);
        }
        {
            var Q0;
            Q0=makeQuery(id+"F81.imprint","IMPRINT",FACE,{"disambiguationData":[TD([[makeQuery(id+"F81.imprint","IMPRINT",EDGE,{"derivedFrom":sQuery(id+"F81.wireOp",EDGE,"E116.sketch_text.stroke-9")}),-1.0]])]});
            var Q1;
            Q1=makeQuery(id+"F81.imprint","IMPRINT",FACE,{"disambiguationData":[TD([[makeQuery(id+"F81.imprint","IMPRINT",EDGE,{"derivedFrom":sQuery(id+"F81.wireOp",EDGE,"E116.sketch_text.stroke-0")}),-1.0]])]});
            extrude(context, id + "F83", {"entities" : qUnion([Q0, Q1]), "operationType" : NewBodyOperationType.REMOVE, "oppositeDirection" : true, "depth" : 0.25 * mm});
        }
        {
            var Q0;
            Q0=makeQuery(id+"F82.imprint","IMPRINT",FACE,{"disambiguationData":[TD([[makeQuery(id+"F82.imprint","IMPRINT",EDGE,{"derivedFrom":sQuery(id+"F82.wireOp",EDGE,"E117.sketch_text.stroke-0")}),-1.0]])]});
            var Q1;
            Q1=makeQuery(id+"F82.imprint","IMPRINT",FACE,{"disambiguationData":[TD([[makeQuery(id+"F82.imprint","IMPRINT",EDGE,{"derivedFrom":sQuery(id+"F82.wireOp",EDGE,"E117.sketch_text.stroke-9")}),-1.0]])]});
            extrude(context, id + "F84", {"entities" : qUnion([Q0, Q1]), "operationType" : NewBodyOperationType.REMOVE, "oppositeDirection" : true, "depth" : 0.25 * mm});
        }
        {
            var Q0;
            Q0=makeQuery(id+"F71.imprint","IMPRINT",FACE,{"disambiguationData":[TD([[makeQuery(id+"F71.imprint","IMPRINT",EDGE,{"derivedFrom":sQuery(id+"F71.wireOp",EDGE,"E106.sketch_text.stroke-0")}),-1.0]])]});
            var Q1;
            Q1=makeQuery(id+"F71.imprint","IMPRINT",FACE,{"disambiguationData":[TD([[makeQuery(id+"F71.imprint","IMPRINT",EDGE,{"derivedFrom":sQuery(id+"F71.wireOp",EDGE,"E106.sketch_text.stroke-9")}),-1.0]])]});
            extrude(context, id + "F85", {"entities" : qUnion([Q0, Q1]), "operationType" : NewBodyOperationType.REMOVE, "oppositeDirection" : true, "depth" : 0.25 * mm});
        }
        {
            var Q0;
            Q0=makeQuery(id+"F73.imprint","IMPRINT",FACE,{"disambiguationData":[TD([[makeQuery(id+"F73.imprint","IMPRINT",EDGE,{"derivedFrom":sQuery(id+"F73.wireOp",EDGE,"E108.sketch_text.stroke-0")}),-1.0]])]});
            extrude(context, id + "F86", {"entities" : qUnion([Q0]), "operationType" : NewBodyOperationType.REMOVE, "oppositeDirection" : true, "depth" : 0.25 * mm});
        }
        {
            var Q0;
            Q0=makeQuery(id+"F74.imprint","IMPRINT",FACE,{"disambiguationData":[TD([[makeQuery(id+"F74.imprint","IMPRINT",EDGE,{"derivedFrom":sQuery(id+"F74.wireOp",EDGE,"E109.sketch_text.stroke-0")}),-1.0]])]});
            extrude(context, id + "F87", {"entities" : qUnion([Q0]), "operationType" : NewBodyOperationType.REMOVE, "oppositeDirection" : true, "depth" : 0.25 * mm});
        }
        {
            var Q0;
            Q0=makeQuery(id+"F75.imprint","IMPRINT",FACE,{"disambiguationData":[TD([[makeQuery(id+"F75.imprint","IMPRINT",EDGE,{"derivedFrom":sQuery(id+"F75.wireOp",EDGE,"E110.sketch_text.stroke-0")}),-1.0]])]});
            extrude(context, id + "F88", {"entities" : qUnion([Q0]), "operationType" : NewBodyOperationType.REMOVE, "oppositeDirection" : true, "depth" : 0.25 * mm});
        }
        {
            var Q0;
            Q0=makeQuery(id+"F77.imprint","IMPRINT",FACE,{"disambiguationData":[TD([[makeQuery(id+"F77.imprint","IMPRINT",EDGE,{"derivedFrom":sQuery(id+"F77.wireOp",EDGE,"E112.sketch_text.stroke-0")}),-1.0]])]});
            var Q1;
            Q1=makeQuery(id+"F77.imprint","IMPRINT",FACE,{"disambiguationData":[TD([[makeQuery(id+"F77.imprint","IMPRINT",EDGE,{"derivedFrom":sQuery(id+"F77.wireOp",EDGE,"E112.sketch_text.stroke-25")}),-1.0]])]});
            extrude(context, id + "F89", {"entities" : qUnion([Q0, Q1]), "operationType" : NewBodyOperationType.REMOVE, "oppositeDirection" : true, "depth" : 0.25 * mm});
        }
        {
            var Q0;
            Q0=makeQuery(id+"F79.imprint","IMPRINT",FACE,{"disambiguationData":[TD([[makeQuery(id+"F79.imprint","IMPRINT",EDGE,{"derivedFrom":sQuery(id+"F79.wireOp",EDGE,"E114.sketch_text.stroke-0")}),-1.0]])]});
            extrude(context, id + "F90", {"entities" : qUnion([Q0]), "operationType" : NewBodyOperationType.REMOVE, "oppositeDirection" : true, "depth" : 0.25 * mm});
        }
        {
            var Q0;
            Q0=makeQuery(id+"F69.imprint","IMPRINT",FACE,{"disambiguationData":[TD([[makeQuery(id+"F69.imprint","IMPRINT",EDGE,{"derivedFrom":sQuery(id+"F69.wireOp",EDGE,"E105.sketch_text.stroke-0")}),-1.0]])]});
            var Q1;
            Q1=makeQuery(id+"F69.imprint","IMPRINT",FACE,{"disambiguationData":[TD([[makeQuery(id+"F69.imprint","IMPRINT",EDGE,{"derivedFrom":sQuery(id+"F69.wireOp",EDGE,"E105.sketch_text.stroke-9")}),-1.0]])]});
            extrude(context, id + "F91", {"entities" : qUnion([Q0, Q1]), "operationType" : NewBodyOperationType.REMOVE, "oppositeDirection" : true, "depth" : 0.28 * mm});
        }
        {
            var Q0;
            Q0=makeQuery(id+"F80.imprint","IMPRINT",FACE,{"disambiguationData":[TD([[makeQuery(id+"F80.imprint","IMPRINT",EDGE,{"derivedFrom":sQuery(id+"F80.wireOp",EDGE,"E115.sketch_text.stroke-9")}),-1.0]])]});
            var Q1;
            Q1=makeQuery(id+"F80.imprint","IMPRINT",FACE,{"disambiguationData":[TD([[makeQuery(id+"F80.imprint","IMPRINT",EDGE,{"derivedFrom":sQuery(id+"F80.wireOp",EDGE,"E115.sketch_text.stroke-0")}),-1.0]])]});
            extrude(context, id + "F92", {"entities" : qUnion([Q0, Q1]), "operationType" : NewBodyOperationType.REMOVE, "oppositeDirection" : true, "depth" : 0.25 * mm});
        }
        {
            var Q0;
            Q0=makeQuery(id+"F65.imprint","IMPRINT",FACE,{"disambiguationData":[TD([[makeQuery(id+"F65.imprint","IMPRINT",EDGE,{"derivedFrom":sQuery(id+"F65.wireOp",EDGE,"E101.sketch_text.stroke-9")}),-1.0]])]});
            var Q1;
            Q1=makeQuery(id+"F65.imprint","IMPRINT",FACE,{"disambiguationData":[TD([[makeQuery(id+"F65.imprint","IMPRINT",EDGE,{"derivedFrom":sQuery(id+"F65.wireOp",EDGE,"E101.sketch_text.stroke-0")}),-1.0]])]});
            extrude(context, id + "F93", {"entities" : qUnion([Q0, Q1]), "operationType" : NewBodyOperationType.REMOVE, "oppositeDirection" : true, "depth" : 0.25 * mm});
        }
        {
            var Q0;
            Q0=makeQuery(id+"F66.imprint","IMPRINT",FACE,{"disambiguationData":[TD([[makeQuery(id+"F66.imprint","IMPRINT",EDGE,{"derivedFrom":sQuery(id+"F66.wireOp",EDGE,"E102.sketch_text.stroke-0")}),-1.0]])]});
            var Q1;
            Q1=makeQuery(id+"F66.imprint","IMPRINT",FACE,{"disambiguationData":[TD([[makeQuery(id+"F66.imprint","IMPRINT",EDGE,{"derivedFrom":sQuery(id+"F66.wireOp",EDGE,"E102.sketch_text.stroke-9")}),-1.0]])]});
            extrude(context, id + "F94", {"entities" : qUnion([Q0, Q1]), "operationType" : NewBodyOperationType.REMOVE, "oppositeDirection" : true, "depth" : 0.25 * mm});
        }
        {
            var Q0;
            Q0=makeQuery(id+"F62.imprint","IMPRINT",FACE,{"disambiguationData":[TD([[makeQuery(id+"F62.imprint","IMPRINT",EDGE,{"derivedFrom":sQuery(id+"F62.wireOp",EDGE,"E98.sketch_text.stroke-0")}),-1.0]])]});
            var Q1;
            Q1=makeQuery(id+"F62.imprint","IMPRINT",FACE,{"disambiguationData":[TD([[makeQuery(id+"F62.imprint","IMPRINT",EDGE,{"derivedFrom":sQuery(id+"F62.wireOp",EDGE,"E98.sketch_text.stroke-20")}),-1.0]])]});
            extrude(context, id + "F95", {"entities" : qUnion([Q0, Q1]), "operationType" : NewBodyOperationType.REMOVE, "oppositeDirection" : true, "depth" : 0.25 * mm});
        }
        {
            var Q0;
            Q0=makeQuery(id+"F64.imprint","IMPRINT",FACE,{"disambiguationData":[TD([[makeQuery(id+"F64.imprint","IMPRINT",EDGE,{"derivedFrom":sQuery(id+"F64.wireOp",EDGE,"E100.sketch_text.stroke-9")}),-1.0]])]});
            var Q1;
            Q1=makeQuery(id+"F64.imprint","IMPRINT",FACE,{"disambiguationData":[TD([[makeQuery(id+"F64.imprint","IMPRINT",EDGE,{"derivedFrom":sQuery(id+"F64.wireOp",EDGE,"E100.sketch_text.stroke-0")}),-1.0]])]});
            extrude(context, id + "F96", {"entities" : qUnion([Q0, Q1]), "operationType" : NewBodyOperationType.REMOVE, "oppositeDirection" : true, "depth" : 0.25 * mm});
        }
        {
            var Q0;
            Q0=makeQuery(id+"F63.imprint","IMPRINT",FACE,{"disambiguationData":[TD([[makeQuery(id+"F63.imprint","IMPRINT",EDGE,{"derivedFrom":sQuery(id+"F63.wireOp",EDGE,"E99.sketch_text.stroke-0")}),-1.0]])]});
            var Q1;
            Q1=makeQuery(id+"F63.imprint","IMPRINT",FACE,{"disambiguationData":[TD([[makeQuery(id+"F63.imprint","IMPRINT",EDGE,{"derivedFrom":sQuery(id+"F63.wireOp",EDGE,"E99.sketch_text.stroke-9")}),-1.0]])]});
            extrude(context, id + "F97", {"entities" : qUnion([Q0, Q1]), "operationType" : NewBodyOperationType.REMOVE, "oppositeDirection" : true, "depth" : 0.25 * mm});
        }
        {
            var Q0;
            Q0=makeQuery(id+"F68.imprint","IMPRINT",FACE,{"disambiguationData":[TD([[makeQuery(id+"F68.imprint","IMPRINT",EDGE,{"derivedFrom":sQuery(id+"F68.wireOp",EDGE,"E104.sketch_text.stroke-9")}),-1.0]])]});
            var Q1;
            Q1=makeQuery(id+"F68.imprint","IMPRINT",FACE,{"disambiguationData":[TD([[makeQuery(id+"F68.imprint","IMPRINT",EDGE,{"derivedFrom":sQuery(id+"F68.wireOp",EDGE,"E104.sketch_text.stroke-0")}),-1.0]])]});
            extrude(context, id + "F98", {"entities" : qUnion([Q0, Q1]), "operationType" : NewBodyOperationType.REMOVE, "oppositeDirection" : true, "depth" : 0.25 * mm});
        }
        {
            var Q0;
            Q0=makeQuery(id+"F78.imprint","IMPRINT",FACE,{"disambiguationData":[TD([[makeQuery(id+"F78.imprint","IMPRINT",EDGE,{"derivedFrom":sQuery(id+"F78.wireOp",EDGE,"E113.sketch_text.stroke-0")}),-1.0]])]});
            var Q1;
            Q1=makeQuery(id+"F78.imprint","IMPRINT",FACE,{"disambiguationData":[TD([[makeQuery(id+"F78.imprint","IMPRINT",EDGE,{"derivedFrom":sQuery(id+"F78.wireOp",EDGE,"E113.sketch_text.stroke-26")}),-1.0]])]});
            extrude(context, id + "F99", {"entities" : qUnion([Q0, Q1]), "operationType" : NewBodyOperationType.REMOVE, "oppositeDirection" : true, "depth" : 0.25 * mm});
        }
        {
            var Q0;
            Q0=makeQuery(id+"F72.imprint","IMPRINT",FACE,{"disambiguationData":[TD([[makeQuery(id+"F72.imprint","IMPRINT",EDGE,{"derivedFrom":sQuery(id+"F72.wireOp",EDGE,"E107.sketch_text.stroke-0")}),-1.0]])]});
            extrude(context, id + "F100", {"entities" : qUnion([Q0]), "operationType" : NewBodyOperationType.REMOVE, "oppositeDirection" : true, "depth" : 0.25 * mm});
        }
        {
            var Q0;
            Q0=makeQuery(id+"F76.imprint","IMPRINT",FACE,{"disambiguationData":[TD([[makeQuery(id+"F76.imprint","IMPRINT",EDGE,{"derivedFrom":sQuery(id+"F76.wireOp",EDGE,"E111.sketch_text.stroke-0")}),-1.0]])]});
            extrude(context, id + "F101", {"entities" : qUnion([Q0]), "operationType" : NewBodyOperationType.REMOVE, "oppositeDirection" : true, "depth" : 0.25 * mm});
        }
        {
            var Q0;
            Q0=makeQuery(id+"F67.imprint","IMPRINT",FACE,{"disambiguationData":[TD([[makeQuery(id+"F67.imprint","IMPRINT",EDGE,{"derivedFrom":sQuery(id+"F67.wireOp",EDGE,"E103.sketch_text.stroke-0")}),-1.0]])]});
            extrude(context, id + "F102", {"entities" : qUnion([Q0]), "operationType" : NewBodyOperationType.REMOVE, "oppositeDirection" : true, "depth" : 0.25 * mm});
        }
        {
            var Q0;
            Q0=qCreatedBy(makeId("Top.planeOp"),FACE);
            cPlane(context, id + "F103", {"entities" : qUnion([Q0]), "cplaneType" : CPlaneType.OFFSET, "offset" : 7.72 * mm, "width" : 152.4 * mm, "height" : 152.4 * mm});
        }
    });
